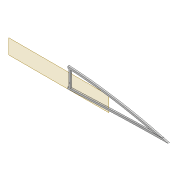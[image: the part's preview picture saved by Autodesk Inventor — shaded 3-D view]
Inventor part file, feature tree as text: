
AUTODESK INVENTOR PART (.ipt)
format: ipt  version: 2022 (Build 260153000, 153)  size: 416,768 bytes
history: native  units: mm
features: extrude x9, sketch x7, projected_geometry x5, fillet x2, shell x1, plane x1
ambient origin geometry x8: Origin, YZ Plane, XZ Plane, XY Plane, X Axis, Y Axis, Z Axis, Center Point
bodies: Solid1 (feature_tree)
feature tree (25):
  extrude  "Extrusion1"  Depth=5.0mm
  shell  "Shell1"  Thickness=2.0mm
  extrude  "Extrusion8"  Depth=5.9mm
  extrude  "Extrusion3"  Depth=10.0mm TaperAngle=0.0deg
  extrude  "Extrusion4"  Depth=2.0mm
  fillet  "Fillet1"  Radius=5.0mm
  sketch  "Sketch10"  dims[d22=4.0mm d23=0.0mm d31=2.0mm d32=5.0mm]
  extrude  "Extrusion5"  Depth=2.5mm
  plane  "Work Plane2"
  extrude  "Extrusion9"  Depth=1.6mm
  extrude  "Extrusion10"  Depth=80.0mm
  fillet  "Fillet2"  Radius=6.0mm
  extrude  "Extrusion11"  Depth=4.0mm TaperAngle=0.0deg
  extrude  "Extrusion12"  Depth=3.0mm
  sketch  "Sketch3"  dims[d0=4.0mm d1=0.0mm d2=5.0mm d7=2.0mm]
  sketch  "Sketch8"  dims[d8=2.0mm d9=5.9mm]
  sketch  "Sketch9"  dims[d13=10.0mm d14=0.0mm d16=10.0mm d17=0.0mm]
  projected_geometry  "Projected Loop4"
  projected_geometry  "Projected Loop10"
  sketch  "Sketch24"  dims[d34=1.6mm d35=2.5mm]
  projected_geometry  "Projected Loop11"
  projected_geometry  "Projected Loop12"
  sketch  "Sketch26"  dims[d37=5.0mm d38=1.6mm]
  projected_geometry  "Projected Loop13"
  sketch  "Sketch27"  dims[d40=2.5mm d62=80.0mm d63=6.0mm d64=4.0mm d65=0.0mm d66=3.0mm d67=12.0mm d68=5.0mm d69=22.0mm d70=12.0mm d71=3.05mm d72=4.0mm d73=0.0mm d74=10.0mm d75=0.0mm d76=2.0mm d77=100.0mm d78=20.0mm d79=0.5mm d80=10.0mm d81=0.0mm d82=10.0mm d83=0.0mm]
